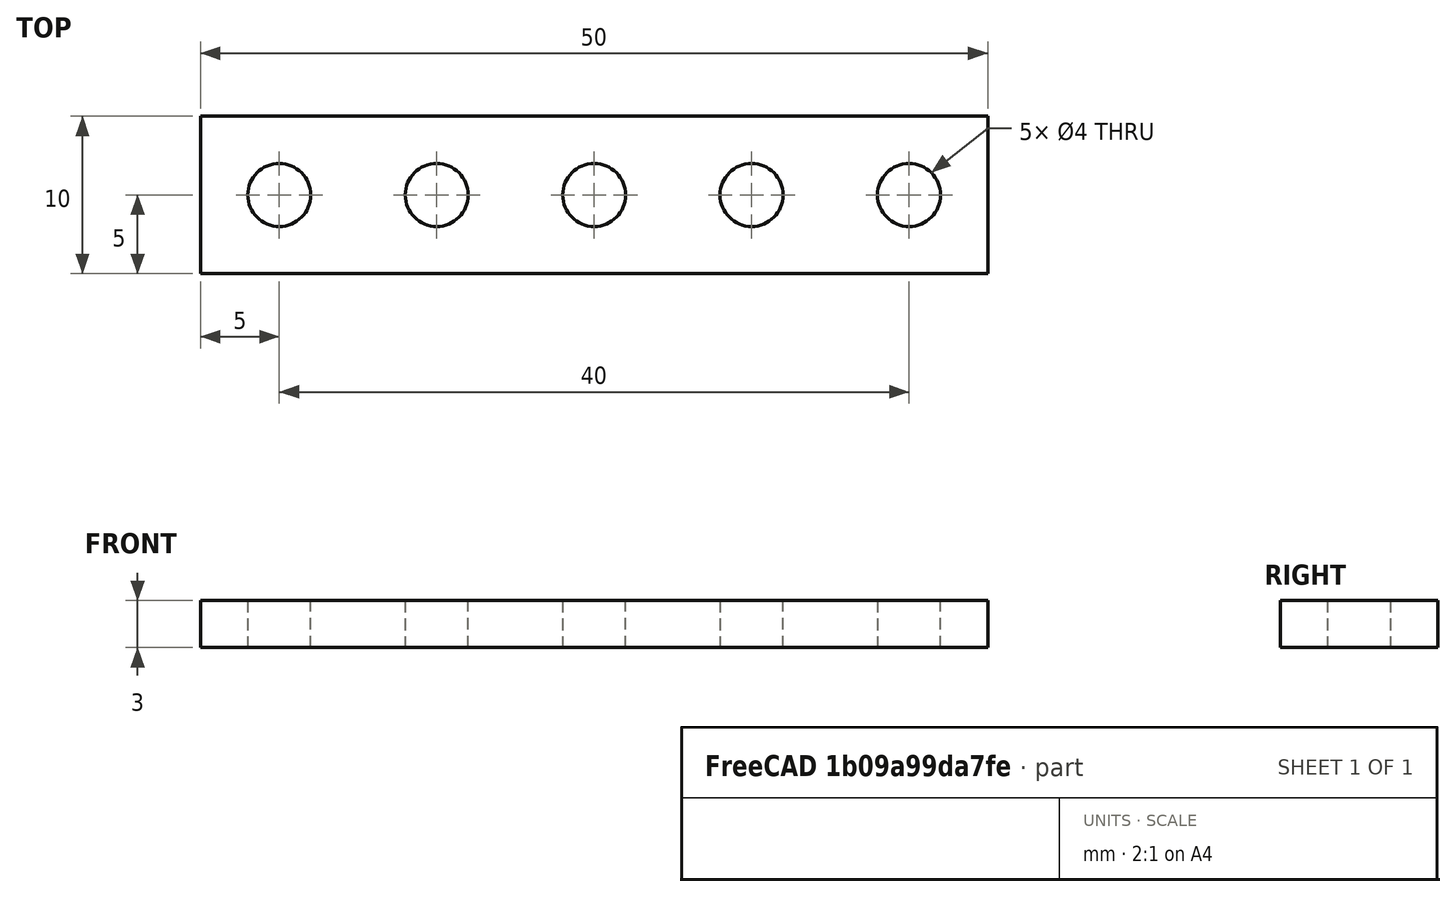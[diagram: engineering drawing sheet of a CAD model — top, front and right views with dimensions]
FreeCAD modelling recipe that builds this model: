
FCSTD DOCUMENT  (FreeCAD 0.20R29177 +233 (Git))
Label: pieza-mecano
License: Creative Commons Attribution-ShareAlike
LicenseURL: http://creativecommons.org/licenses/by-sa/4.0/
objects: Part::Cylinder×5, Part::Cut×5, Part::Box×1
note: 11 computed .brp shape members not serialized (recipe doc carries the construction recipe); baked Part::Feature solids carry a one-line shape summary decoded from their .brp

FEATURE [Part::Box] Box  label="Cubo"
  AttacherType = Attacher::AttachEngine3D
  Height = 3
  Length = 50
  Width = 10
FEATURE [Part::Cylinder] Cylinder  label="Cilindro"
  Angle = 360
  AttacherType = Attacher::AttachEngine3D
  FirstAngle = 0
  Height = 10
  Placement = pos=(5,5,0) rot=(0,0,1;0rad)
  Radius = 2
  SecondAngle = 0
FEATURE [Part::Cylinder] Cylinder001  label="Cilindro001"
  Angle = 360
  AttacherType = Attacher::AttachEngine3D
  FirstAngle = 0
  Height = 10
  Placement = pos=(15,5,0) rot=(0,0,1;0rad)
  Radius = 2
  SecondAngle = 0
FEATURE [Part::Cylinder] Cylinder002  label="Cilindro002"
  Angle = 360
  AttacherType = Attacher::AttachEngine3D
  FirstAngle = 0
  Height = 10
  Placement = pos=(25,5,0) rot=(0,0,1;0rad)
  Radius = 2
  SecondAngle = 0
FEATURE [Part::Cylinder] Cylinder003  label="Cilindro003"
  Angle = 360
  AttacherType = Attacher::AttachEngine3D
  FirstAngle = 0
  Height = 10
  Placement = pos=(35,5,0) rot=(0,0,1;0rad)
  Radius = 2
  SecondAngle = 0
FEATURE [Part::Cylinder] Cylinder004  label="Cilindro004"
  Angle = 360
  AttacherType = Attacher::AttachEngine3D
  FirstAngle = 0
  Height = 10
  Placement = pos=(45,5,0) rot=(0,0,1;0rad)
  Radius = 2
  SecondAngle = 0
FEATURE [Part::Cut] Cut
  Base = -> Box
  Refine = true
  Tool = -> Cylinder
FEATURE [Part::Cut] Cut001
  Base = -> Cut
  Refine = true
  Tool = -> Cylinder001
FEATURE [Part::Cut] Cut002
  Base = -> Cut001
  Refine = true
  Tool = -> Cylinder002
FEATURE [Part::Cut] Cut003
  Base = -> Cut002
  Refine = true
  Tool = -> Cylinder003
FEATURE [Part::Cut] Cut004
  Base = -> Cut003
  Refine = true
  Tool = -> Cylinder004
